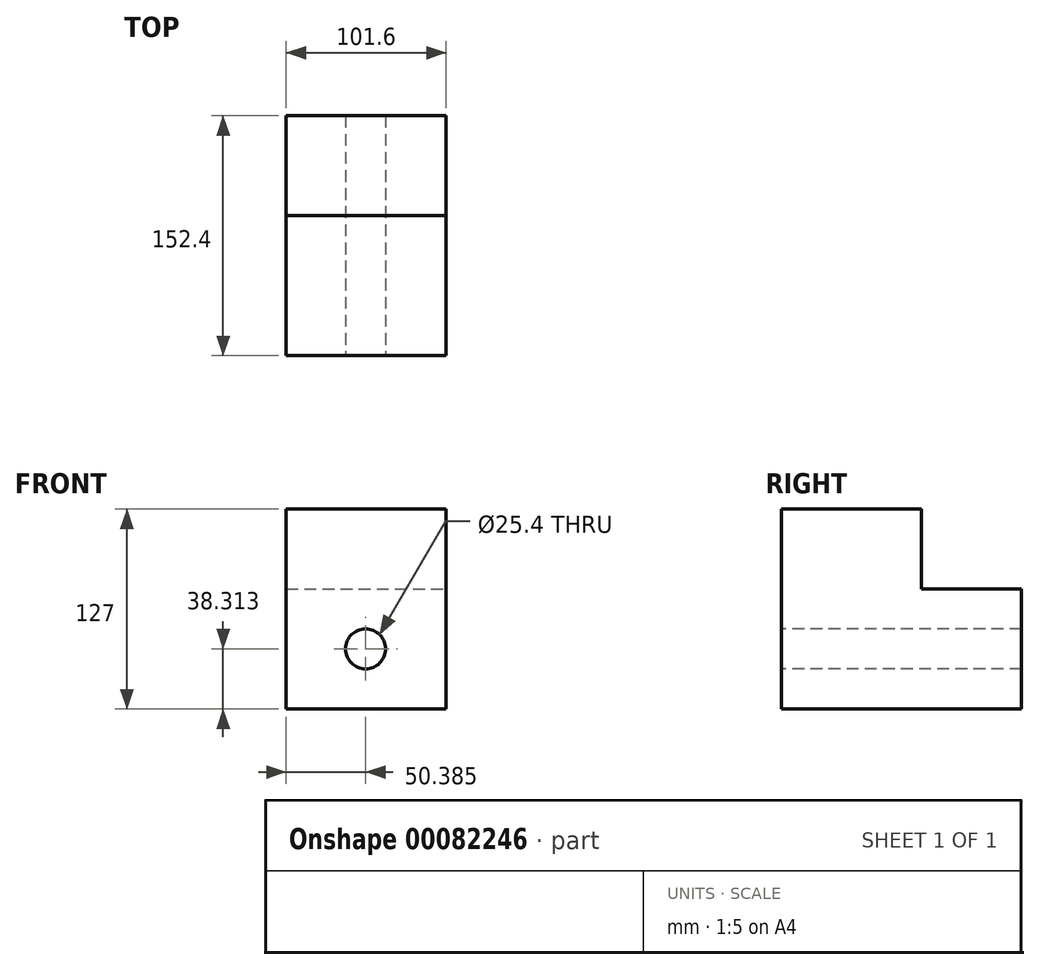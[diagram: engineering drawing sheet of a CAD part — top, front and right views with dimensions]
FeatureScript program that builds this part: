
annotation { "Feature Type Name" : "Feature", "Feature Type Description" : "" }
export const myFeature = defineFeature(function(context is Context, id is Id, definition is map)
    precondition{}
    {
        {
            var Q0;
            Q0=qCreatedBy(makeId("Top.planeOp"),FACE);
            var sketch = newSketch(context, id + "F0", { "sketchPlane" : qUnion([Q0])});
            skLineSegment(sketch, "E0", {"start": v(0, 0) * mm, "end": v(0, 152.4) * mm});
            skLineSegment(sketch, "E1", {"start": v(0, 152.4) * mm, "end": v(-101.6, 152.4) * mm});
            skLineSegment(sketch, "E2", {"start": v(-101.6, 152.4) * mm, "end": v(-101.6, 0) * mm});
            skLineSegment(sketch, "E3", {"start": v(-101.6, 0) * mm, "end": v(0, 0) * mm});
            skSolve(sketch);
        }
        {
            var Q0;
            Q0 = qSketchRegion(id + "F0", true);
            var Q1;
            Q1 = qSketchRegion(id + "FM14ZapKSvBw0VN_1", true);
            extrude(context, id + "F1", {"entities" : qUnion([Q0, Q1]), "depth" : 127 * mm});
        }
        {
            var Q0;
            Q0=makeQuery(id+"F1.opExtrude","SWEPT_FACE",FACE,{"disambiguationData":[OSD([sQuery(id+"F0.wireOp",EDGE,"E0")])]});
            var sketch = newSketch(context, id + "F2", { "sketchPlane" : qUnion([Q0])});
            skLineSegment(sketch, "E4.bottom", {"start": v(152.4, 127) * mm, "end": v(88.9, 127) * mm});
            skLineSegment(sketch, "E4.top", {"start": v(152.4, 76.2) * mm, "end": v(88.9, 76.2) * mm});
            skLineSegment(sketch, "E4.left", {"start": v(152.4, 127) * mm, "end": v(152.4, 76.2) * mm});
            skLineSegment(sketch, "E4.right", {"start": v(88.9, 127) * mm, "end": v(88.9, 76.2) * mm});
            skSolve(sketch);
        }
        {
            var Q0;
            Q0 = qSketchRegion(id + "F2", true);
            extrude(context, id + "F3", {"entities" : qUnion([Q0]), "operationType" : NewBodyOperationType.REMOVE, "endBound" : BoundingType.THROUGH_ALL, "oppositeDirection" : true, "depth" : 25.4 * mm});
        }
        {
            var Q0;
            Q0=makeQuery(id+"F1.opExtrude","SWEPT_FACE",FACE,{"disambiguationData":[OSD([sQuery(id+"F0.wireOp",EDGE,"E3")])]});
            var sketch = newSketch(context, id + "F4", { "sketchPlane" : qUnion([Q0])});
            skLineSegment(sketch, "E5.bottom", {"start": v(-101.6, 0) * mm, "end": v(-50.8, 0) * mm});
            skLineSegment(sketch, "E5.top", {"start": v(-101.6, 38.1) * mm, "end": v(-50.8, 38.1) * mm});
            skLineSegment(sketch, "E5.left", {"start": v(-101.6, 0) * mm, "end": v(-101.6, 38.1) * mm});
            skLineSegment(sketch, "E5.right", {"start": v(-50.8, 0) * mm, "end": v(-50.8, 38.1) * mm});
            skSolve(sketch);
        }
        {
            var Q0;
            Q0=makeQuery(id+"F4.imprint","IMPRINT",FACE,{"disambiguationData":[TD([[makeQuery(id+"F4.imprint","IMPRINT",EDGE,{"derivedFrom":sQuery(id+"F4.wireOp",EDGE,"E5.bottom")}),1.0]])]});
            var sketch = newSketch(context, id + "F5", { "sketchPlane" : qUnion([Q0])});
            skCircle(sketch, "E6", {"center": v(-51.22, 38.31) * mm, "radius": 12.7 * mm});
            skSolve(sketch);
        }
        {
            var Q0;
            Q0 = qSketchRegion(id + "F5", true);
            extrude(context, id + "F6", {"entities" : qUnion([Q0]), "operationType" : NewBodyOperationType.REMOVE, "endBound" : BoundingType.THROUGH_ALL, "oppositeDirection" : true, "depth" : 25.4 * mm});
        }
    });
